# Revit family: Asma klozet için Geberit Kombifix elemanı, 109 cm, Alpha 8 cm gömme rezervuar ile, destek ayakları ile_PRO_182342
name_source: partatom
category: Plumbing Fixtures
units: mm (PartAtom-declared; Revit-internal decimal feet)

## family parameters
Always vertical = Yes
Cut with Voids When Loaded = No
OmniClass Number = 23.31.00.00
Part Type = Normal
Room Calculation Point = Yes
Round Connector Dimension = Use Diameter
Shared = No
Work Plane-Based = No

## types (1)
- 110.174.00.1 Asma klozet için Geberit Kombifix elemanı, 109 cm, Alpha 8 cm gömme rezervuar ile, destek ayakları ile
    Application purposes = Tuğla duvarlar için
Yarım veya oda yüksekliğinde duvar önü montaj için
Bağlantı ölçüleri EN 33:2011 standardına uygun asma klozetler için
2 kademeli deşarj için
    Application range = sanitary systems
    Article number key = 110.174.00.1
    B = 420 mm  [stored 1.37795 ft]
    BIM Content Version = GEB MG 1.5
    BIM Content revision date = 2024.01.26
    Brand = Geberit
    Büyük yıkama miktarı ayar aralığı (l) = 4 / 4.5 / 6 / 7.5 l
    CW Connection = Yes
    Characteristics = Montaj çerçevesi galvanizli
Dört montaj kulakçıklı
Sıva taşıyıcı doku önceden monte edilmiştir
Montaj dirseği, duvar kalınlığı 8 veya 12 cm olan tuğla duvarlarla uyumludur
Sifon dirseği sabitlemesi takımsız
Önden basmalı gömme rezervuar
Yoğuşmaya karşı izolasyonlu gömme rezervuar
Fabrika ayarında hızlı ilave drenaj mümkündür
Su bağlantısı üstte solda
Servis açıklığı şablon kutusu kısaltılabilir
    Connection description 1 = cold water in
    Connection description 2 = sanitary out
    Default Elevation = 0 mm  [stored 0 ft]
    Description = Asma klozet için Geberit Kombifix elemanı, 109 cm, Alpha 8 cm gömme rezervuar ile, destek ayakları ile
    EAN code = 4025416497660
    EAN code basic data = 4025416497660
    GEB_culture = tr-TR
    GEB_generic_description = concealed cistern support frame for toilet
    GEB_generic_manufacturer = generic
    GEB_imperial_engineering = No
    GEB_metric_engineering = Yes
    GEB_pimversion = 24.02.14
    GEB_processing_type = T
    GEB_reference = PRO_182342
    GEB_translations = {"GEB_connection_diameter1":"Connection diameter 1","GEB_connection_diameter2":"Connection diameter 2","application_range":"Application range","applicationPurposes":"Application purposes","ATT_10673":"EAN code basic data","ATT_10773":"Çalışma basıncı","ATT_10866":"Yıkama miktarı fabrika ayarı","ATT_10807":"Büyük yıkama miktarı ayar aralığı (l)","ATT_10811":"Küçük yıkama miktarı ayar aralığı","brandName":"Brand","characteristics":"Characteristics","connection_description1":"Connection description 1","connection_description2":"Connection description 2","connection_type_c01":"Connection type at connection 01","connection_type_c02":"Connection type at connection 02","content_creator":"BIM Content creator","content_date_changed":"BIM Content revision date","content_version":"BIM Content Version","name":"Name","productBrand":"Product brand","scopeOfDelivery":"Scope of delivery","type":"Type","angle":"Angle","GEB_cut_length_c02":"Max cutting length at connection 02","sanitary socket":"Adapter socket","rod spacing 180mm":"Fastening distance 180mm","rod spacing 230mm":"Fastening distance 230mm","warning":"Warning","fixed_material":"Main material","fixed_material_01":"Main material 01","fixed_material_02":"Main material 02","fixed_material_04":"Main material 04","fixed_material_03":"Main material 03","key 1000":"Article number key","key 3000":"EAN code"}
    GEB_use_DN = Yes
    H = 1090 mm  [stored 3.57612 ft]
    H1 = 230 mm  [stored 0.754593 ft]
    H2 = 330 mm  [stored 1.08268 ft]
    HW Connection = No
    HWFU = 0
    IfcDescription = Asma klozet için Geberit Kombifix elemanı, 109 cm, Alpha 8 cm gömme rezervuar ile, destek ayakları ile
    IfcExportAs = IfcSanitaryTerminal
    IfcExportType = CISTERN
    Küçük yıkama miktarı ayar aralığı = 2-4 l
    LOD300 = No
    LOD400 = Yes
    Main material = Geberit, Plastic, Opaque white
    Main material 01 = Geberit, Steel, Paint Finish, Blue
    Main material 02 = Geberit, Laminate, Ivory, Matte
    Main material 03 = Geberit, Steel, galvanized
    Main material 04 = Geberit, PE-HD, Black
    Manufacturer = Geberit
    Model = Alpha 8 cm
    Name = Asma klozet için Geberit Kombifix elemanı, 109 cm, Alpha 8 cm gömme rezervuar ile, destek ayakları ile
    Product brand = Kombifix
    Scope of delivery = Su bağlantısı R 1/2", MF uyumlu, entegre ara musluklu ve el volanlı
Servis açıklığı için şablon kutusu
4 montaj dirsekler
Klozet bağlantı seti, ø 90 mm
Sifon dirseği PE-HD, ø 90 mm
PE-HD geçiş mufu, ø 90 / 110 mm
2 koruyucu tapa
2 dişli rot M12
Ayaklar seti
Sabitleme malzemesi
    T = 80 mm  [stored 0.262467 ft]
    Type = Alpha 8 cm
    Vent Connection = No
    Waste Connection = Yes
    Yıkama miktarı fabrika ayarı = 6 ve 3 l
    adapter_socket_included = Yes
    connection_bend_included = Yes
    cw_h = 45 mm  [stored 0.147638 ft]
    inlet_flow = 0.1 L/s
    outlet_flow = 0.0 L/s
    rod_width_180 = 180 mm  [stored 0.590551 ft]
    rod_width_230 = 230 mm  [stored 0.754593 ft]
    use_SoD_csv = Yes
    Çalışma basıncı = 0.1-10 bar

note: [stored X ft] marks values corroborated as IEEE doubles in the binary element streams (Revit-internal decimal feet)

## geometry (parser evidence)
native form markers: Blend x2, Sweep x3
no freeform markers — native parametric forms only
